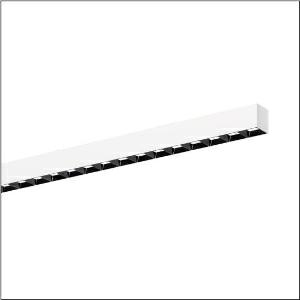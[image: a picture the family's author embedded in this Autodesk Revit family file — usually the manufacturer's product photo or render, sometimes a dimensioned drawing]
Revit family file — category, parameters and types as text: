
# Revit family: silica_r__21_51mx21da34wb_4769
name_source: partatom
category: Lighting Fixtures
units: mm (PartAtom-declared; Revit-internal decimal feet)

## family parameters
Cut with Voids When Loaded = No
Host = Face
Light Source = No
Part Type = Normal
Room Calculation Point = No
Round Connector Dimension = Use Diameter
Shared = No

## types (1)
- --- (1 x LED, 4320 lm, 27.4 W, 3000K)
    Apparent Load = 27 VA
    CIE Flux Codes = 87 99 100 100 100
    Color Rendering = 80
    Color Temperature = 3000K
    Default Elevation = 1800 mm
    Description = Silica® 21, office luminaire, primary light control with darklight reflector, of PMMA, black, CAT 2 (L<= 3000cd/m²), light emission: direct distribution, primary light characteristic: symmetric, installation type: surface-mounted, LED, rated luminous flux: 4.320lm, luminous efficacy: 158lm/W, light colour: 830, colour temperature: 3000K, with terminal, 3+2-pole, max. 2.5mm², mains connection: 220..240V, AC, 50/60Hz, rated input power: 27.4W, luminaire housing, of aluminium, traffic white (RAL 9016), length: 1.204mm, width: 53mm, height: 53mm, protection rating (complete): IP20, insulation class (complete): insulation class I (protective earthing), certification: CE, permissible operating ambient temperature: 0..+35°C, standard: EN 50419, packaging unit: 1 piece
    Height = 0 mm  [stored 0 ft]
    Lamp = 1 x LED
    Lamp Light Flux = 4320 lm
    Lamp Power = 27.4 W
    Lamp count = 1
    Length = 1204 mm
    Luminous efficacy = 158 lm/W
    Manufacturer = Siteco
    ModVariant = No
    Model = 51MX21DA34WB
    Mounting Place = Ceiling
    Mounting Type = Recessed
    Number of Poles = 1
    OnlyDefault = Yes
    Power Factor = 1
    Product Name = Silica® 21
    Product group = office luminaire | ceiling recessed
    ProductGroupID = 401
    Protection Class = Protection class I
    Protection Degree = IP 20
    RLX_Detail_Level = 1
    RLX_Emergency_Light_Flux = 0 lm
    RLX_Emergency_Type = 0
    RLX_Emergency_Type_DB = No
    RlxData = <blob elided: 41149 chars, md5=4d9adc50>
    Socket = socket
    Standby Power = 0 W
    System Light Flux = 4320 lm
    System Power = 27 W
    Type Comments = factory setting: luminous flux: 100 % | dim-lin: 254 | 393 mA
    Type Image = l_1297779.jpg
    URL = http://relux.com
    VarID = @adj_054947
    Voltage = 0 V
    Weight = 0.00 kg
    Width = 53 mm

note: [stored X ft] marks values corroborated as IEEE doubles in the binary element streams (Revit-internal decimal feet)

## geometry (parser evidence)
native form markers: Blend x4, Sweep x12
no freeform markers — native parametric forms only
